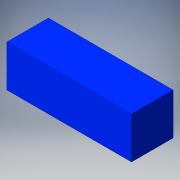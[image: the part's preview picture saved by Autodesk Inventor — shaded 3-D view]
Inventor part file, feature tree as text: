
AUTODESK INVENTOR PART (.ipt)
format: ipt  version: 2016 (Build 200138000, 138)  size: 96,256 bytes
history: native  units: in
note: dims shown in document units (in); Inventor stores cm internally (conversion verified against a paired STEP export)
features: extrude x1, sketch x1
ambient origin geometry x8: Origin, YZ Plane, XZ Plane, XY Plane, X Axis, Y Axis, Z Axis, Center Point
bodies: Solid1 (feature_tree)
feature tree (2):
  extrude  "Extrusion1"  Depth=1.0in
  sketch  "Sketch1"  dims[d0=3.0in d1=1.0in d2=1.0in d3=0.0in]
